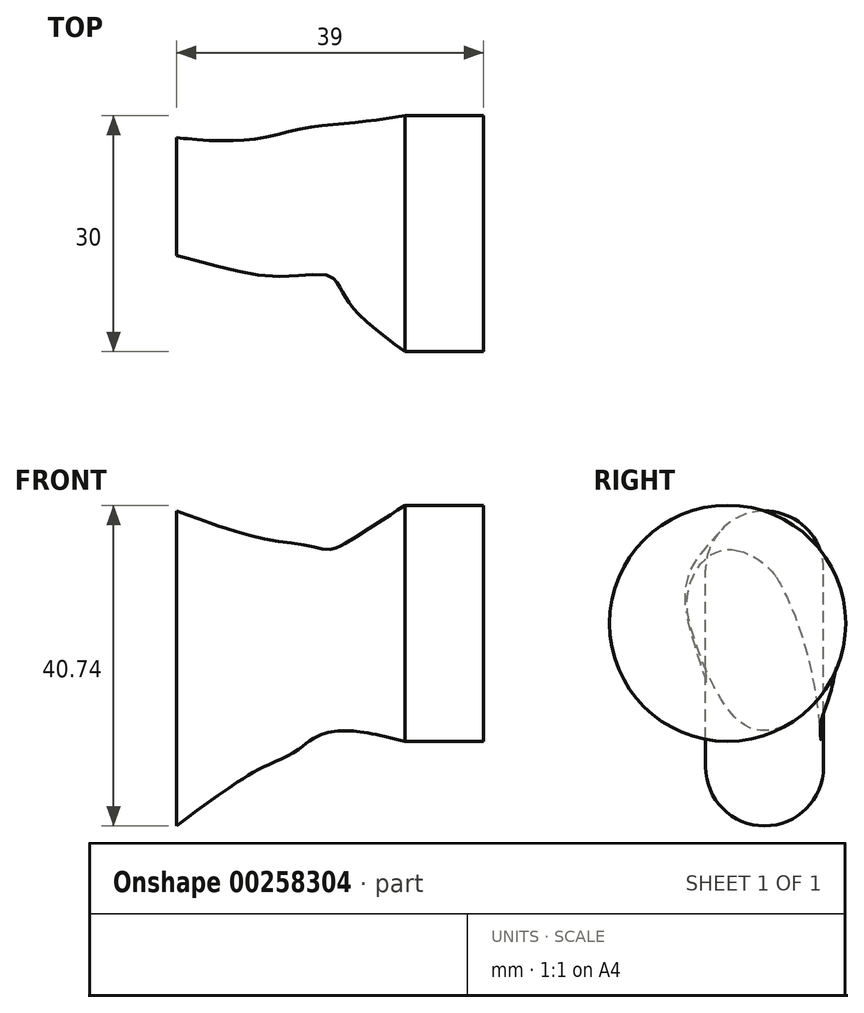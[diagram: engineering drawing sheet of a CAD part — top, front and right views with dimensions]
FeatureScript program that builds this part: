
annotation { "Feature Type Name" : "Feature", "Feature Type Description" : "" }
export const myFeature = defineFeature(function(context is Context, id is Id, definition is map)
    precondition{}
    {
        {
            var Q0;
            Q0=qCreatedBy(makeId("Right.planeOp"),FACE);
            cPlane(context, id + "F0", {"entities" : qUnion([Q0]), "cplaneType" : CPlaneType.OFFSET, "offset" : 29 * mm, "oppositeDirection" : true, "width" : 150 * mm, "height" : 150 * mm});
        }
        {
            var Q0;
            Q0=qCreatedBy(makeId("Right.planeOp"),FACE);
            var sketch = newSketch(context, id + "F1", { "sketchPlane" : qUnion([Q0])});
            skCircle(sketch, "E0", {"center": v(0, 0) * mm, "radius": 15 * mm});
            skSolve(sketch);
        }
        {
            var Q0;
            Q0=makeQuery(id+"F1.imprint","IMPRINT",FACE,{"disambiguationData":[TD([[makeQuery(id+"F1.imprint","IMPRINT",EDGE,{"derivedFrom":sQuery(id+"F1.wireOp",EDGE,"E0")}),1.0]])]});
            extrude(context, id + "F2", {"entities" : qUnion([Q0]), "depth" : 10 * mm, "offsetDistance" : 25 * mm});
        }
        {
            var Q0;
            Q0=qCreatedBy(id+"F0.planeOp",FACE);
            var sketch = newSketch(context, id + "F3", { "sketchPlane" : qUnion([Q0])});
            skLineSegment(sketch, "E1.bottom", {"start": v(-2.8, -18.24) * mm, "end": v(12.2, -18.24) * mm, "construction": true});
            skLineSegment(sketch, "E1.top", {"start": v(-2.8, 6.76) * mm, "end": v(12.2, 6.76) * mm, "construction": true});
            skLineSegment(sketch, "E1.left", {"start": v(-2.8, -18.24) * mm, "end": v(-2.8, 6.76) * mm});
            skLineSegment(sketch, "E1.right", {"start": v(12.2, -18.24) * mm, "end": v(12.2, 6.76) * mm});
            skPoint(sketch, "E1.middle", {"position": v(4.7, -5.74) * mm});
            skArc(sketch, "E2", {"start": v(12.2, 6.76) * mm, "mid": v(4.7, 14.26) * mm, "end": v(-2.8, 6.76) * mm});
            skArc(sketch, "E3", {"start": v(-2.8, -18.24) * mm, "mid": v(4.7, -25.74) * mm, "end": v(12.2, -18.24) * mm});
            skSolve(sketch);
        }
        {
            var Q0;
            Q0=qCreatedBy(makeId("Right.planeOp"),FACE);
            var sketch = newSketch(context, id + "F4", { "sketchPlane" : qUnion([Q0])});
            skArc(sketch, "E4", {"start": v(14.36, 4.34) * mm, "mid": v(1.85, 14.89) * mm, "end": v(-12.86, 7.72) * mm});
            skArc(sketch, "E5", {"start": v(-12.86, 7.72) * mm, "mid": v(-14.84, -2.2) * mm, "end": v(-10.08, -11.11) * mm});
            skArc(sketch, "E6", {"start": v(-10.08, -11.11) * mm, "mid": v(-0.1, -15) * mm, "end": v(9.92, -11.25) * mm});
            skArc(sketch, "E7", {"start": v(9.92, -11.25) * mm, "mid": v(14.43, -4.1) * mm, "end": v(14.36, 4.34) * mm});
            skSolve(sketch);
        }
        {
            var Q0;
            Q0=qCreatedBy(makeId("Top.planeOp"),FACE);
            var sketch = newSketch(context, id + "F5", { "sketchPlane" : qUnion([Q0])});
            skFitSpline(sketch, "E8", {"points": [v(-29, -2.8) * mm, v(-15.4, -10.5) * mm, v(0, -15) * mm], "startDerivative": vector(30.54, -0.37) * mm, "endDerivative": vector(40.37, -0.66) * mm});
            skFitSpline(sketch, "E9", {"points": [v(-29, 12.2) * mm, v(-17.02, 13.6) * mm, v(0, 15) * mm], "startDerivative": vector(38.52, 0.03) * mm, "endDerivative": vector(68.56, -3.22) * mm});
            skSolve(sketch);
        }
        {
            var Q0;
            Q0=sQuery(id+"F5.wireOp",EDGE,"E9");
            var Q1;
            Q1=makeQuery(id+"F3.imprint","IMPRINT",FACE,{"disambiguationData":[TD([[makeQuery(id+"F3.imprint","IMPRINT",EDGE,{"derivedFrom":sQuery(id+"F3.wireOp",EDGE,"E1.left")}),-1.0]])]});
            var Q2;
            Q2=makeQuery(id+"F2.opExtrude","CAP_FACE",FACE,{"disambiguationData":[OSD([sQuery(id+"F1.wireOp",EDGE,"E0")])],"isStart":true});
            var Q3;
            Q3=sQuery(id+"F3.wireOp",VERTEX,"E1.bottom.start");
            var Q4;
            Q4=sQuery(id+"F4.wireOp",VERTEX,"E6.end");
            loft(context, id + "F6", {"addSections" : true, "spine" : qUnion([Q0]), "sectionCount" : 5, "sheetProfilesArray" : [{ "sheetProfileEntities" : qUnion([Q1]) }, { "sheetProfileEntities" : qUnion([Q2]) }], "matchConnections" : true, "connections" : [{ "connectionEntities" : qUnion([Q3, Q4]), "connectionEdgeQueries" : qUnion([]), "connectionEdgeParameters" : [] }]});
        }
    });
